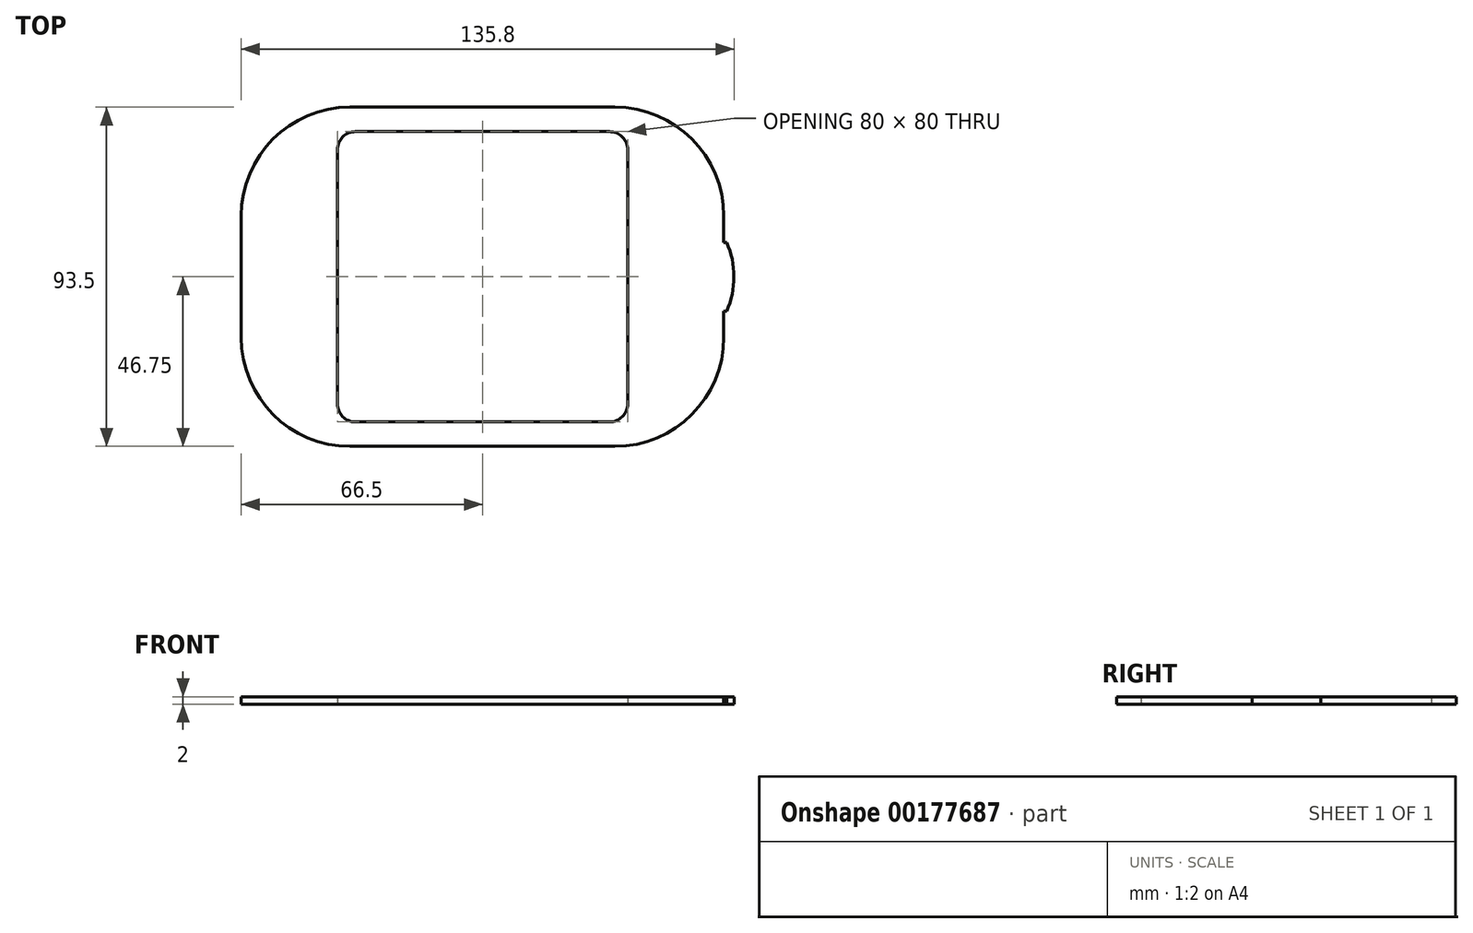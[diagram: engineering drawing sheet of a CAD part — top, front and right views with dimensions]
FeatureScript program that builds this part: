
annotation { "Feature Type Name" : "Feature", "Feature Type Description" : "" }
export const myFeature = defineFeature(function(context is Context, id is Id, definition is map)
    precondition{}
    {
        {
            var Q0;
            Q0=qCreatedBy(makeId("Top.planeOp"),FACE);
            var sketch = newSketch(context, id + "F0", { "sketchPlane" : qUnion([Q0])});
            skLineSegment(sketch, "E0.bottom", {"start": v(36.5, 46.75) * mm, "end": v(-36.5, 46.75) * mm});
            skLineSegment(sketch, "E0.top", {"start": v(36.5, -46.75) * mm, "end": v(-36.5, -46.75) * mm});
            skLineSegment(sketch, "E0.left", {"start": v(66.5, 16.75) * mm, "end": v(66.5, -16.75) * mm});
            skLineSegment(sketch, "E0.right", {"start": v(-66.5, 16.75) * mm, "end": v(-66.5, -16.75) * mm});
            skPoint(sketch, "E0.middle", {"position": v(0, 0) * mm});
            skLineSegment(sketch, "E1.bottom", {"start": v(35, 40) * mm, "end": v(-35, 40) * mm});
            skLineSegment(sketch, "E1.top", {"start": v(35, -40) * mm, "end": v(-35, -40) * mm});
            skLineSegment(sketch, "E1.left", {"start": v(40, 35) * mm, "end": v(40, -35) * mm});
            skLineSegment(sketch, "E1.right", {"start": v(-40, 35) * mm, "end": v(-40, -35) * mm});
            skPoint(sketch, "E2.visualSharp", {"position": v(-66.5, -46.75) * mm});
            skArc(sketch, "E2.filletArc", {"start": v(-66.5, -16.75) * mm, "mid": v(-57.71, -37.96) * mm, "end": v(-36.5, -46.75) * mm});
            skPoint(sketch, "E3.visualSharp", {"position": v(66.5, -46.75) * mm});
            skArc(sketch, "E3.filletArc", {"start": v(36.5, -46.75) * mm, "mid": v(57.71, -37.96) * mm, "end": v(66.5, -16.75) * mm});
            skPoint(sketch, "E4.visualSharp", {"position": v(66.5, 46.75) * mm});
            skArc(sketch, "E4.filletArc", {"start": v(66.5, 16.75) * mm, "mid": v(57.71, 37.96) * mm, "end": v(36.5, 46.75) * mm});
            skPoint(sketch, "E5.visualSharp", {"position": v(-66.5, 46.75) * mm});
            skArc(sketch, "E5.filletArc", {"start": v(-36.5, 46.75) * mm, "mid": v(-57.71, 37.96) * mm, "end": v(-66.5, 16.75) * mm});
            skLineSegment(sketch, "E6.bottom", {"start": v(-66.5, 9.5) * mm, "end": v(-69.3, 9.5) * mm});
            skLineSegment(sketch, "E6.top", {"start": v(-66.5, -9.5) * mm, "end": v(-69.3, -9.5) * mm});
            skLineSegment(sketch, "E6.left", {"start": v(-66.5, 9.5) * mm, "end": v(-66.5, -9.5) * mm});
            skLineSegment(sketch, "E6.right", {"start": v(-69.3, 9.5) * mm, "end": v(-69.3, -9.5) * mm});
            skPoint(sketch, "E7", {"position": v(-67.3, 9.5) * mm});
            skPoint(sketch, "E8", {"position": v(-67.3, -9.5) * mm});
            skPoint(sketch, "E9", {"position": v(-69.3, 0) * mm});
            skArc(sketch, "E10", {"start": v(-67.3, 9.5) * mm, "mid": v(-69.3, 0) * mm, "end": v(-67.3, -9.5) * mm});
            skLineSegment(sketch, "E11.MirrorCS", {"start": v(66.5, 9.5) * mm, "end": v(69.3, 9.5) * mm});
            skLineSegment(sketch, "E12.MirrorCS", {"start": v(69.3, 9.5) * mm, "end": v(69.3, -9.5) * mm});
            skLineSegment(sketch, "E13.MirrorCS", {"start": v(66.5, -9.5) * mm, "end": v(69.3, -9.5) * mm});
            skArc(sketch, "E14.MirrorCS", {"start": v(67.3, 9.5) * mm, "mid": v(69.3, 0) * mm, "end": v(67.3, -9.5) * mm});
            skPoint(sketch, "E15.visualSharp", {"position": v(-40, -40) * mm});
            skArc(sketch, "E15.filletArc", {"start": v(-40, -35) * mm, "mid": v(-38.54, -38.54) * mm, "end": v(-35, -40) * mm});
            skPoint(sketch, "E16.visualSharp", {"position": v(-40, 40) * mm});
            skArc(sketch, "E16.filletArc", {"start": v(-35, 40) * mm, "mid": v(-38.54, 38.54) * mm, "end": v(-40, 35) * mm});
            skPoint(sketch, "E17.visualSharp", {"position": v(40, 40) * mm});
            skArc(sketch, "E17.filletArc", {"start": v(40, 35) * mm, "mid": v(38.54, 38.54) * mm, "end": v(35, 40) * mm});
            skPoint(sketch, "E18.visualSharp", {"position": v(40, -40) * mm});
            skArc(sketch, "E18.filletArc", {"start": v(35, -40) * mm, "mid": v(38.54, -38.54) * mm, "end": v(40, -35) * mm});
            skSolve(sketch);
        }
        {
            var Q0;
            Q0=makeQuery(id+"F0.imprint","IMPRINT",FACE,{"disambiguationData":[TD([[makeQuery(id+"F0.imprint","IMPRINT",EDGE,{"derivedFrom":sQuery(id+"F0.wireOp",EDGE,"E0.bottom")}),1.0]])]});
            var Q1;
            {var subQ1=sQuery(id+"F0.wireOp",EDGE,"E11.MirrorCS");var subQ4=sQuery(id+"F0.wireOp",EDGE,"E0.left");var subQ5=makeQuery(id+"F0.imprint","INTERSECT",VERTEX,{"derivedFrom":[subQ4,subQ1]});Q1=makeQuery(id+"F0.imprint","IMPRINT",FACE,{"disambiguationData":[TD([[makeQuery(id+"F0.imprint","IMPRINT",EDGE,{"disambiguationData":[TD([[subQ5,-1.0]])],"derivedFrom":subQ4}),1.0]])]});}
            var Q2;
            {var subQ6=sQuery(id+"F0.wireOp",EDGE,"E6.left");Q2=makeQuery(id+"F0.imprint","IMPRINT",FACE,{"disambiguationData":[TD([[makeQuery(id+"F0.imprint","IMPRINT",EDGE,{"derivedFrom":subQ6}),-1.0]])]});}
            extrude(context, id + "F1", {"entities" : qUnion([Q0, Q1, Q2]), "depth" : 2 * mm});
        }
    });
